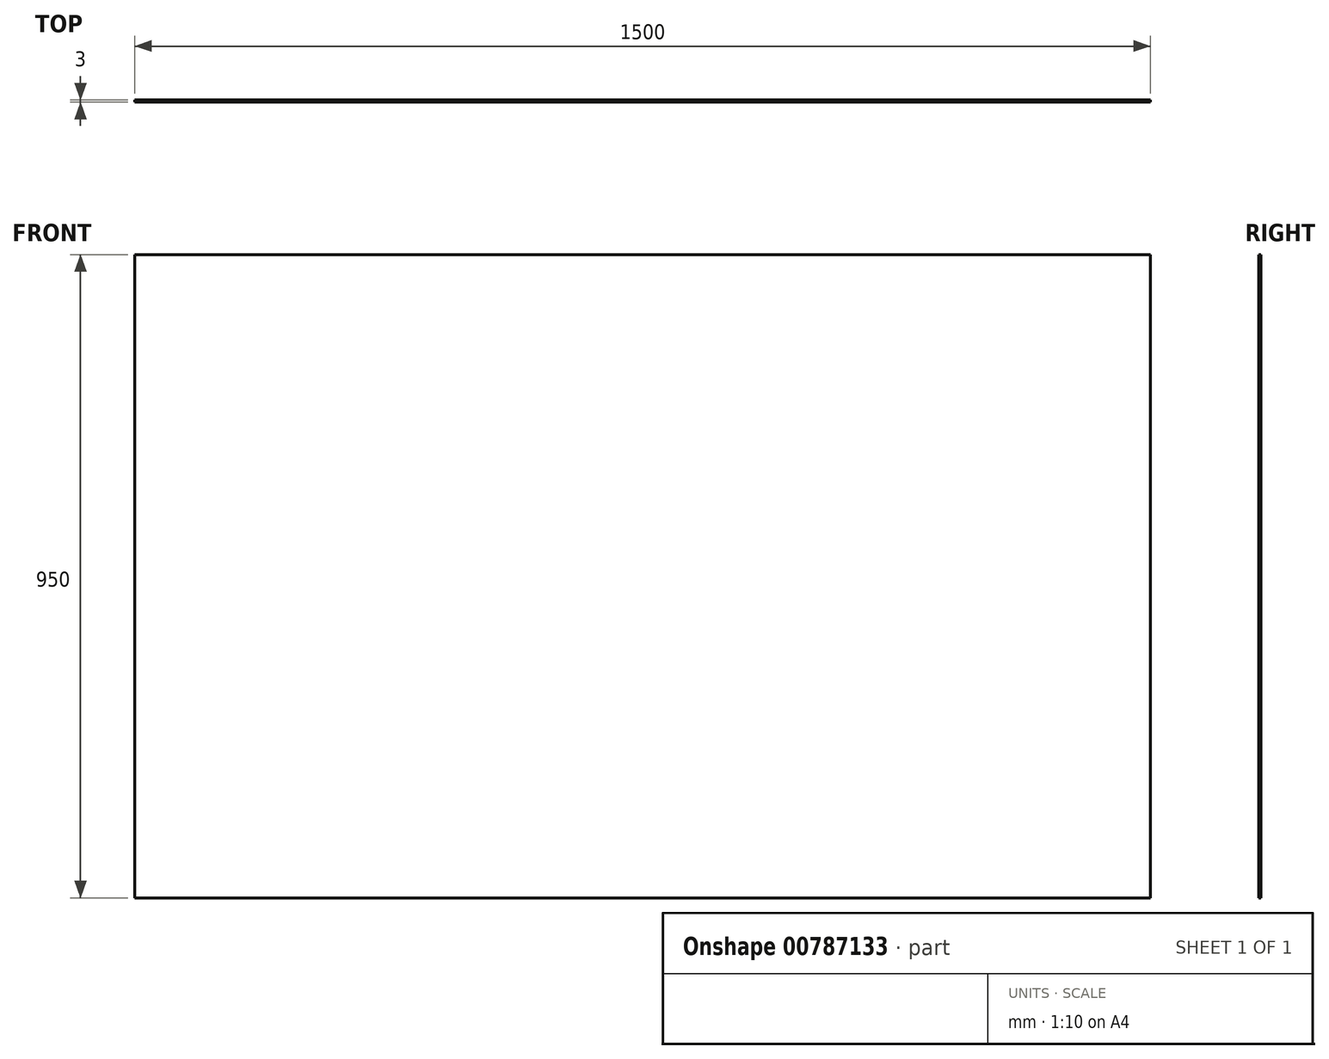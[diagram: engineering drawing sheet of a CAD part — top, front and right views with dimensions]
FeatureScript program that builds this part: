
annotation { "Feature Type Name" : "Feature", "Feature Type Description" : "" }
export const myFeature = defineFeature(function(context is Context, id is Id, definition is map)
    precondition{}
    {
        {
            var Q0;
            Q0=qCreatedBy(makeId("Front.planeOp"),FACE);
            var sketch = newSketch(context, id + "F0", { "sketchPlane" : qUnion([Q0])});
            skLineSegment(sketch, "E0.bottom", {"start": v(750, 475) * mm, "end": v(-750, 475) * mm});
            skLineSegment(sketch, "E0.top", {"start": v(750, -475) * mm, "end": v(-750, -475) * mm});
            skLineSegment(sketch, "E0.left", {"start": v(750, 475) * mm, "end": v(750, -475) * mm});
            skLineSegment(sketch, "E0.right", {"start": v(-750, 475) * mm, "end": v(-750, -475) * mm});
            skPoint(sketch, "E0.middle", {"position": v(0, 0) * mm});
            skSolve(sketch);
        }
        {
            var Q0;
            Q0=makeQuery(id+"F0.imprint","IMPRINT",FACE,{"disambiguationData":[TD([[makeQuery(id+"F0.imprint","IMPRINT",EDGE,{"derivedFrom":sQuery(id+"F0.wireOp",EDGE,"E0.bottom")}),1.0]])]});
            extrude(context, id + "F1", {"entities" : qUnion([Q0]), "depth" : 3 * mm, "offsetDistance" : 25 * mm});
        }
    });
